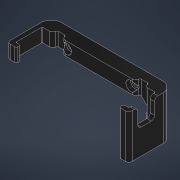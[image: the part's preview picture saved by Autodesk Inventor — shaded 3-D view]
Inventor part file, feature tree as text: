
AUTODESK INVENTOR PART (.ipt)
format: ipt  version: 2021 (Build 250183000, 183)  size: 306,176 bytes
history: native  units: mm
features: fillet x9, extrude x7, other x6, chamfer x3, reference x2, hole x2, plane x1, projected_geometry x1
ambient origin geometry x8: Origin, YZ Plane, XZ Plane, XY Plane, X Axis, Y Axis, Z Axis, Center Point
bodies: Solid1 (feature_tree)
feature tree (31):
  plane  "Work Plane1"
  extrude  "base"  Depth=67.0mm
  extrude  "holes_bolt_head"  Depth=38.0mm
  fillet  "bolt_head_fillet"  Radius=19.0mm
  other  "walls_sketch"
  extrude  "wall"  Depth=4.0mm
  extrude  "wall_offset_top"  Depth=4.0mm
  extrude  "wall_offset_bottom"  Depth=8.0mm TaperAngle=0.0deg
  fillet  "wall_top"  Radius=5.8mm
  fillet  "wall_tooth"  Radius=5.8mm
  chamfer  "wall_bottom"  Distance=3.2mm
  fillet  "inside"  Radius=0.5mm
  fillet  "bottom"  Radius=15.7mm
  chamfer  "wall_offset_outside"  Distance=3.0mm
  chamfer  "l_corner"  Angle=360.0deg  [1 undecoded]
  fillet  "wall_offset_rounding"  Radius=2.6mm
  extrude  "hole_usb_c"  Depth=2.6mm
  fillet  "hole_usb_c_rounded"  Radius=3.0mm
  fillet  "wall_offset_inside"  Radius=2.0mm
  extrude  "groove_enclosure_bolt"  Depth=1.0mm
  fillet  "groove_enclosure_bolt_rounded"  Radius=2.0mm
  other  "base_sketch"
  reference  "Reference1"
  reference  "Reference2"
  hole  "holes_bolt_head_sketch"  [1 undecoded]
  projected_geometry  "Projected Loop1"
  hole  "hole_usb_c_sketch"  [1 undecoded]
  other  "groove_enclosure_bolt_sketch"
  parser-record x1  (decoder bookkeeping rows leaked as tree rows — omitted from the tree; the rows remain in map.json)
  other  "plate_electronics.iam"
  other  "plate:1"
note: 3 required parameter values undecoded (feature->parameter linkage not recoverable at this tier; creation-order binding heuristic only, values carry confidence <= 0.55)
note: 1 file-system path scrubbed to <path> (originals preserved in map.json)
